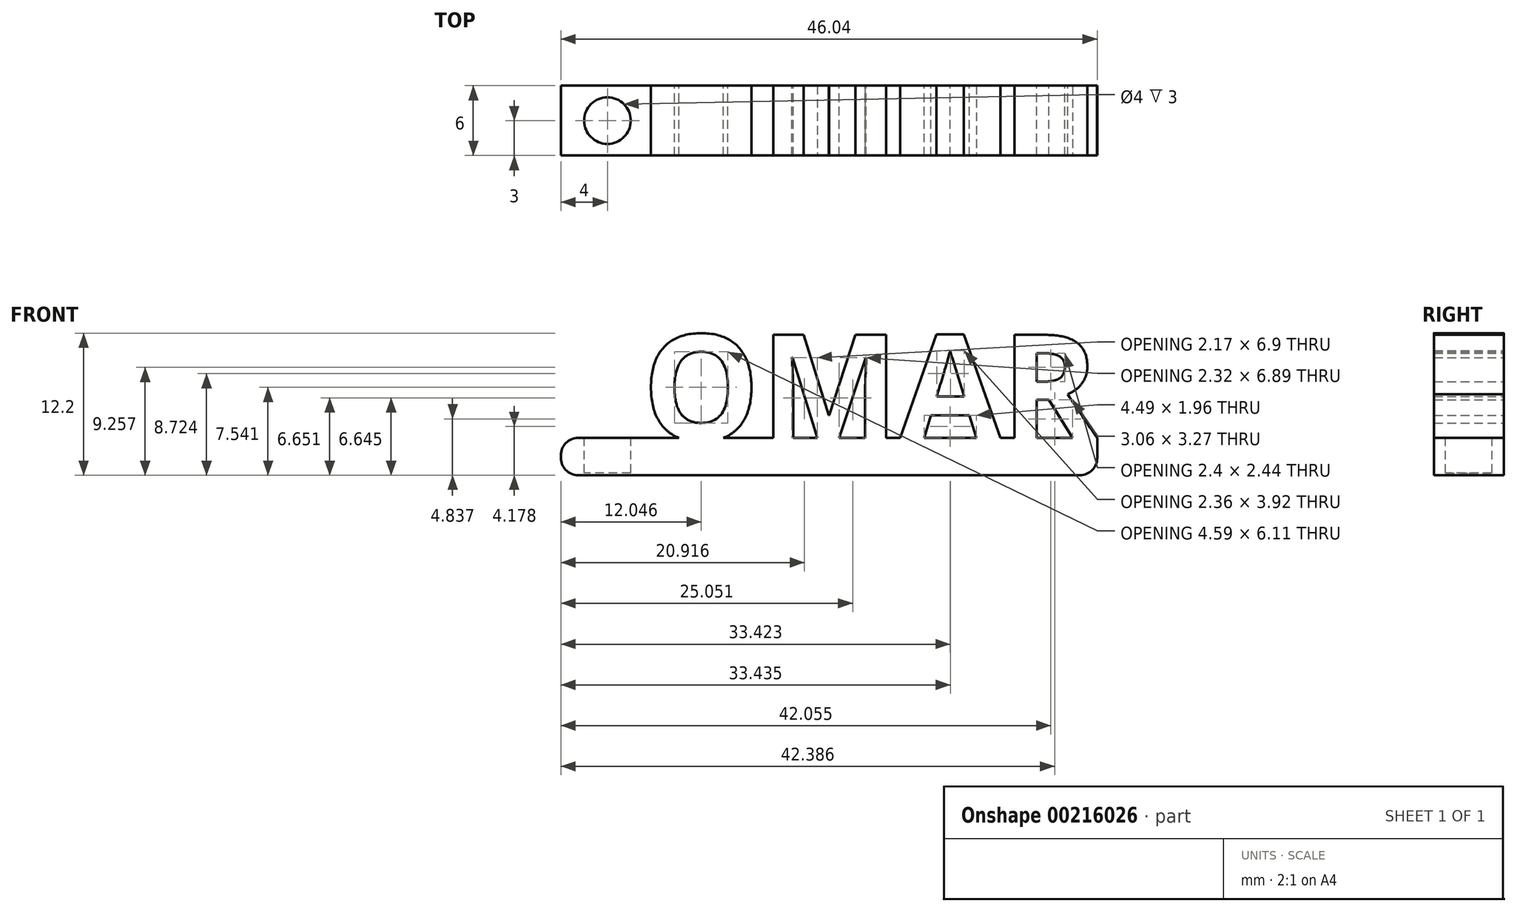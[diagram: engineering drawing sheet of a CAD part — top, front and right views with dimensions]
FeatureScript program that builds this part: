
annotation { "Feature Type Name" : "Feature", "Feature Type Description" : "" }
export const myFeature = defineFeature(function(context is Context, id is Id, definition is map)
    precondition{}
    {
        {
            var Q0;
            Q0=qCreatedBy(makeId("Front.planeOp"),FACE);
            var sketch = newSketch(context, id + "F0", { "sketchPlane" : qUnion([Q0])});
            skText(sketch, "E0", { "text": "OMAR", "fontName": "OpenSans-Bold.ttf"});
            const initialGuessF0  = {"E0": [-0.02, 0, 1, 0, 0.00913]};
            skSetInitialGuess(sketch, initialGuessF0);
            skSolve(sketch);
        }
        {
            var Q0;
            Q0=qCreatedBy(makeId("Top.planeOp"),FACE);
            var sketch = newSketch(context, id + "F1", { "sketchPlane" : qUnion([Q0])});
            skLineSegment(sketch, "E1.bottom", {"start": v(-20, 3) * mm, "end": v(19.04, 3) * mm});
            skLineSegment(sketch, "E1.top", {"start": v(-20, -3) * mm, "end": v(19.04, -3) * mm});
            skLineSegment(sketch, "E1.left", {"start": v(-20, 3) * mm, "end": v(-20, -3) * mm});
            skLineSegment(sketch, "E1.right", {"start": v(19.04, 3) * mm, "end": v(19.04, -3) * mm});
            skSolve(sketch);
        }
        {
            var Q0;
            Q0 = qSketchRegion(id + "F0", true);
            extrude(context, id + "F2", {"entities" : qUnion([Q0]), "endBound" : BoundingType.SYMMETRIC, "depth" : 6 * mm});
        }
        {
            var Q0;
            Q0=makeQuery(id+"F1.imprint","IMPRINT",FACE,{"disambiguationData":[TD([[makeQuery(id+"F1.imprint","IMPRINT",EDGE,{"derivedFrom":sQuery(id+"F1.wireOp",EDGE,"E1.bottom")}),-1.0]])]});
            extrude(context, id + "F3", {"entities" : qUnion([Q0]), "depth" : 0.2 * mm});
        }
        {
            var Q0;
            Q0=makeQuery(id+"F3.opExtrude","CAP_FACE",FACE,{"disambiguationData":[OSD([sQuery(id+"F1.wireOp",EDGE,"E1.bottom"),sQuery(id+"F1.wireOp",EDGE,"E1.top"),sQuery(id+"F1.wireOp",EDGE,"E1.left"),sQuery(id+"F1.wireOp",EDGE,"E1.right")])],"isStart":true});
            extrude(context, id + "F4", {"entities" : qUnion([Q0]), "depth" : 3 * mm});
        }
        {
            var Q0;
            Q0=makeQuery(id+"F3.opExtrude","SWEPT_BODY",BODY,{"disambiguationData":[OSD([sQuery(id+"F1.wireOp",EDGE,"E1.bottom"),sQuery(id+"F1.wireOp",EDGE,"E1.top"),sQuery(id+"F1.wireOp",EDGE,"E1.left"),sQuery(id+"F1.wireOp",EDGE,"E1.right")])]});
            var Q1;
            Q1=makeQuery(id+"F4.opExtrude","SWEPT_BODY",BODY,{"disambiguationData":[OSD([sQuery(id+"F1.wireOp",EDGE,"E1.bottom"),sQuery(id+"F1.wireOp",EDGE,"E1.top"),sQuery(id+"F1.wireOp",EDGE,"E1.left"),sQuery(id+"F1.wireOp",EDGE,"E1.right")])]});
            var Q2;
            Q2=makeQuery(id+"F2.opExtrude","SWEPT_BODY",BODY,{"disambiguationData":[OSD([sQuery(id+"F0.wireOp",EDGE,"E0.sketch_text.stroke-45"),sQuery(id+"F0.wireOp",EDGE,"E0.sketch_text.stroke-46"),sQuery(id+"F0.wireOp",EDGE,"E0.sketch_text.stroke-47"),sQuery(id+"F0.wireOp",EDGE,"E0.sketch_text.stroke-48"),sQuery(id+"F0.wireOp",EDGE,"E0.sketch_text.stroke-49"),sQuery(id+"F0.wireOp",EDGE,"E0.sketch_text.stroke-50"),sQuery(id+"F0.wireOp",EDGE,"E0.sketch_text.stroke-51"),sQuery(id+"F0.wireOp",EDGE,"E0.sketch_text.stroke-52"),sQuery(id+"F0.wireOp",EDGE,"E0.sketch_text.stroke-53"),sQuery(id+"F0.wireOp",EDGE,"E0.sketch_text.stroke-54"),sQuery(id+"F0.wireOp",EDGE,"E0.sketch_text.stroke-55"),sQuery(id+"F0.wireOp",EDGE,"E0.sketch_text.stroke-56"),sQuery(id+"F0.wireOp",EDGE,"E0.sketch_text.stroke-57"),sQuery(id+"F0.wireOp",EDGE,"E0.sketch_text.stroke-58"),sQuery(id+"F0.wireOp",EDGE,"E0.sketch_text.stroke-59"),sQuery(id+"F0.wireOp",EDGE,"E0.sketch_text.stroke-60"),sQuery(id+"F0.wireOp",EDGE,"E0.sketch_text.stroke-61"),sQuery(id+"F0.wireOp",EDGE,"E0.sketch_text.stroke-62"),sQuery(id+"F0.wireOp",EDGE,"E0.sketch_text.stroke-63")])]});
            var Q3;
            Q3=makeQuery(id+"F2.opExtrude","SWEPT_BODY",BODY,{"disambiguationData":[OSD([sQuery(id+"F0.wireOp",EDGE,"E0.sketch_text.stroke-14"),sQuery(id+"F0.wireOp",EDGE,"E0.sketch_text.stroke-15"),sQuery(id+"F0.wireOp",EDGE,"E0.sketch_text.stroke-16"),sQuery(id+"F0.wireOp",EDGE,"E0.sketch_text.stroke-17"),sQuery(id+"F0.wireOp",EDGE,"E0.sketch_text.stroke-18"),sQuery(id+"F0.wireOp",EDGE,"E0.sketch_text.stroke-19"),sQuery(id+"F0.wireOp",EDGE,"E0.sketch_text.stroke-20"),sQuery(id+"F0.wireOp",EDGE,"E0.sketch_text.stroke-21"),sQuery(id+"F0.wireOp",EDGE,"E0.sketch_text.stroke-22"),sQuery(id+"F0.wireOp",EDGE,"E0.sketch_text.stroke-23"),sQuery(id+"F0.wireOp",EDGE,"E0.sketch_text.stroke-24"),sQuery(id+"F0.wireOp",EDGE,"E0.sketch_text.stroke-25"),sQuery(id+"F0.wireOp",EDGE,"E0.sketch_text.stroke-26"),sQuery(id+"F0.wireOp",EDGE,"E0.sketch_text.stroke-27"),sQuery(id+"F0.wireOp",EDGE,"E0.sketch_text.stroke-28"),sQuery(id+"F0.wireOp",EDGE,"E0.sketch_text.stroke-29"),sQuery(id+"F0.wireOp",EDGE,"E0.sketch_text.stroke-30"),sQuery(id+"F0.wireOp",EDGE,"E0.sketch_text.stroke-31"),sQuery(id+"F0.wireOp",EDGE,"E0.sketch_text.stroke-32")])]});
            var Q4;
            Q4=makeQuery(id+"F2.opExtrude","SWEPT_BODY",BODY,{"disambiguationData":[OSD([sQuery(id+"F0.wireOp",EDGE,"E0.sketch_text.stroke-0"),sQuery(id+"F0.wireOp",EDGE,"E0.sketch_text.stroke-1"),sQuery(id+"F0.wireOp",EDGE,"E0.sketch_text.stroke-2"),sQuery(id+"F0.wireOp",EDGE,"E0.sketch_text.stroke-3"),sQuery(id+"F0.wireOp",EDGE,"E0.sketch_text.stroke-4"),sQuery(id+"F0.wireOp",EDGE,"E0.sketch_text.stroke-5"),sQuery(id+"F0.wireOp",EDGE,"E0.sketch_text.stroke-6"),sQuery(id+"F0.wireOp",EDGE,"E0.sketch_text.stroke-7"),sQuery(id+"F0.wireOp",EDGE,"E0.sketch_text.stroke-8"),sQuery(id+"F0.wireOp",EDGE,"E0.sketch_text.stroke-9"),sQuery(id+"F0.wireOp",EDGE,"E0.sketch_text.stroke-10"),sQuery(id+"F0.wireOp",EDGE,"E0.sketch_text.stroke-11"),sQuery(id+"F0.wireOp",EDGE,"E0.sketch_text.stroke-12"),sQuery(id+"F0.wireOp",EDGE,"E0.sketch_text.stroke-13")])]});
            var Q5;
            Q5=makeQuery(id+"F2.opExtrude","SWEPT_BODY",BODY,{"disambiguationData":[OSD([sQuery(id+"F0.wireOp",EDGE,"E0.sketch_text.stroke-33"),sQuery(id+"F0.wireOp",EDGE,"E0.sketch_text.stroke-34"),sQuery(id+"F0.wireOp",EDGE,"E0.sketch_text.stroke-35"),sQuery(id+"F0.wireOp",EDGE,"E0.sketch_text.stroke-36"),sQuery(id+"F0.wireOp",EDGE,"E0.sketch_text.stroke-37"),sQuery(id+"F0.wireOp",EDGE,"E0.sketch_text.stroke-38"),sQuery(id+"F0.wireOp",EDGE,"E0.sketch_text.stroke-39"),sQuery(id+"F0.wireOp",EDGE,"E0.sketch_text.stroke-40"),sQuery(id+"F0.wireOp",EDGE,"E0.sketch_text.stroke-41"),sQuery(id+"F0.wireOp",EDGE,"E0.sketch_text.stroke-42"),sQuery(id+"F0.wireOp",EDGE,"E0.sketch_text.stroke-43"),sQuery(id+"F0.wireOp",EDGE,"E0.sketch_text.stroke-44")])]});
            booleanBodies(context, id + "F5", {"operationType" : BooleanOperationType.UNION, "tools" : qUnion([Q0, Q1, Q2, Q3, Q4, Q5])});
        }
        {
            var Q0;
            {var subQ0=sQuery(id+"F1.wireOp",EDGE,"E1.left");Q0=makeQuery(id+"F5.opBoolean","MERGE",FACE,{"derivedFrom":[makeQuery(id+"F3.opExtrude","SWEPT_FACE",FACE,{"disambiguationData":[OSD([subQ0])]}),makeQuery(id+"F4.opExtrude","SWEPT_FACE",FACE,{"disambiguationData":[OSD([subQ0])]})]});}
            var sketch = newSketch(context, id + "F6", { "sketchPlane" : qUnion([Q0])});
            skLineSegment(sketch, "E2.bottom", {"start": v(-3, -3) * mm, "end": v(3, -3) * mm});
            skLineSegment(sketch, "E2.top", {"start": v(-3, 0.2) * mm, "end": v(3, 0.2) * mm});
            skLineSegment(sketch, "E2.left", {"start": v(-3, -3) * mm, "end": v(-3, 0.2) * mm});
            skLineSegment(sketch, "E2.right", {"start": v(3, -3) * mm, "end": v(3, 0.2) * mm});
            skSolve(sketch);
        }
        {
            var Q0;
            Q0 = qSketchRegion(id + "F6", true);
            extrude(context, id + "F7", {"entities" : qUnion([Q0]), "operationType" : NewBodyOperationType.ADD, "depth" : 7 * mm});
        }
        {
            var Q0;
            Q0=makeQuery(id+"F7.opExtrude","CAP_EDGE",EDGE,{"disambiguationData":[OSD([sQuery(id+"F6.wireOp",EDGE,"E2.bottom")])],"isStart":false});
            var Q1;
            Q1=makeQuery(id+"F7.opExtrude","CAP_EDGE",EDGE,{"disambiguationData":[OSD([sQuery(id+"F6.wireOp",EDGE,"E2.top")])],"isStart":false});
            var Q2;
            Q2=makeQuery(id+"F4.opExtrude","CAP_EDGE",EDGE,{"disambiguationData":[OSD([sQuery(id+"F1.wireOp",EDGE,"E1.right")])],"isStart":false});
            fillet(context, id + "F8", {"entities" : qUnion([Q0, Q1, Q2]), "radius" : 1.5 * mm, "tangentPropagation" : true, "allowEdgeOverflow" : false});
        }
        {
            var Q0;
            {var subQ19=sQuery(id+"F1.wireOp",EDGE,"E1.top");var subQ20=sQuery(id+"F1.wireOp",EDGE,"E1.bottom");var subQ63=sQuery(id+"F0.wireOp",EDGE,"E0.sketch_text.stroke-2");var subQ66=sQuery(id+"F1.wireOp",EDGE,"E1.left");Q0=makeQuery(id+"F7.boolean.opBoolean","MERGE",FACE,{"derivedFrom":[makeQuery(id+"F5.opBoolean","SPLIT",FACE,{"disambiguationData":[TD([makeQuery(id+"F2.opExtrude","SWEPT_FACE",FACE,{"disambiguationData":[OSD([subQ63])]})])],"derivedFrom":makeQuery(id+"F3.opExtrude","CAP_FACE",FACE,{"disambiguationData":[OSD([subQ20,subQ19,subQ66,sQuery(id+"F1.wireOp",EDGE,"E1.right")])],"isStart":false})}),makeQuery(id+"F7.opExtrude","SWEPT_FACE",FACE,{"disambiguationData":[OSD([sQuery(id+"F6.wireOp",EDGE,"E2.top")])]})]});}
            var sketch = newSketch(context, id + "F9", { "sketchPlane" : qUnion([Q0])});
            skCircle(sketch, "E3", {"center": v(-23, 0) * mm, "radius": 2 * mm});
            skSolve(sketch);
        }
        {
            var Q0;
            Q0=makeQuery(id+"F9.imprint","IMPRINT",FACE,{"disambiguationData":[TD([[makeQuery(id+"F9.imprint","IMPRINT",EDGE,{"derivedFrom":sQuery(id+"F9.wireOp",EDGE,"E3")}),1.0]])]});
            extrude(context, id + "F10", {"entities" : qUnion([Q0]), "operationType" : NewBodyOperationType.REMOVE, "oppositeDirection" : true, "depth" : 3 * mm});
        }
        {
            var Q0;
            {var subQ0=sQuery(id+"F1.wireOp",EDGE,"E1.top");Q0=makeQuery(id+"F7.boolean.opBoolean","MERGE",FACE,{"derivedFrom":[makeQuery(id+"F5.opBoolean","MERGE",FACE,{"derivedFrom":[makeQuery(id+"F2.opExtrude","CAP_FACE",FACE,{"disambiguationData":[OSD([sQuery(id+"F0.wireOp",EDGE,"E0.sketch_text.stroke-0"),sQuery(id+"F0.wireOp",EDGE,"E0.sketch_text.stroke-1"),sQuery(id+"F0.wireOp",EDGE,"E0.sketch_text.stroke-2"),sQuery(id+"F0.wireOp",EDGE,"E0.sketch_text.stroke-3"),sQuery(id+"F0.wireOp",EDGE,"E0.sketch_text.stroke-4"),sQuery(id+"F0.wireOp",EDGE,"E0.sketch_text.stroke-5"),sQuery(id+"F0.wireOp",EDGE,"E0.sketch_text.stroke-6"),sQuery(id+"F0.wireOp",EDGE,"E0.sketch_text.stroke-7"),sQuery(id+"F0.wireOp",EDGE,"E0.sketch_text.stroke-8"),sQuery(id+"F0.wireOp",EDGE,"E0.sketch_text.stroke-9"),sQuery(id+"F0.wireOp",EDGE,"E0.sketch_text.stroke-10"),sQuery(id+"F0.wireOp",EDGE,"E0.sketch_text.stroke-11"),sQuery(id+"F0.wireOp",EDGE,"E0.sketch_text.stroke-12"),sQuery(id+"F0.wireOp",EDGE,"E0.sketch_text.stroke-13")])],"isStart":false}),makeQuery(id+"F2.opExtrude","CAP_FACE",FACE,{"disambiguationData":[OSD([sQuery(id+"F0.wireOp",EDGE,"E0.sketch_text.stroke-14"),sQuery(id+"F0.wireOp",EDGE,"E0.sketch_text.stroke-15"),sQuery(id+"F0.wireOp",EDGE,"E0.sketch_text.stroke-16"),sQuery(id+"F0.wireOp",EDGE,"E0.sketch_text.stroke-17"),sQuery(id+"F0.wireOp",EDGE,"E0.sketch_text.stroke-18"),sQuery(id+"F0.wireOp",EDGE,"E0.sketch_text.stroke-19"),sQuery(id+"F0.wireOp",EDGE,"E0.sketch_text.stroke-20"),sQuery(id+"F0.wireOp",EDGE,"E0.sketch_text.stroke-21"),sQuery(id+"F0.wireOp",EDGE,"E0.sketch_text.stroke-22"),sQuery(id+"F0.wireOp",EDGE,"E0.sketch_text.stroke-23"),sQuery(id+"F0.wireOp",EDGE,"E0.sketch_text.stroke-24"),sQuery(id+"F0.wireOp",EDGE,"E0.sketch_text.stroke-25"),sQuery(id+"F0.wireOp",EDGE,"E0.sketch_text.stroke-26"),sQuery(id+"F0.wireOp",EDGE,"E0.sketch_text.stroke-27"),sQuery(id+"F0.wireOp",EDGE,"E0.sketch_text.stroke-28"),sQuery(id+"F0.wireOp",EDGE,"E0.sketch_text.stroke-29"),sQuery(id+"F0.wireOp",EDGE,"E0.sketch_text.stroke-30"),sQuery(id+"F0.wireOp",EDGE,"E0.sketch_text.stroke-31"),sQuery(id+"F0.wireOp",EDGE,"E0.sketch_text.stroke-32")])],"isStart":false}),makeQuery(id+"F2.opExtrude","CAP_FACE",FACE,{"disambiguationData":[OSD([sQuery(id+"F0.wireOp",EDGE,"E0.sketch_text.stroke-33"),sQuery(id+"F0.wireOp",EDGE,"E0.sketch_text.stroke-34"),sQuery(id+"F0.wireOp",EDGE,"E0.sketch_text.stroke-35"),sQuery(id+"F0.wireOp",EDGE,"E0.sketch_text.stroke-36"),sQuery(id+"F0.wireOp",EDGE,"E0.sketch_text.stroke-37"),sQuery(id+"F0.wireOp",EDGE,"E0.sketch_text.stroke-38"),sQuery(id+"F0.wireOp",EDGE,"E0.sketch_text.stroke-39"),sQuery(id+"F0.wireOp",EDGE,"E0.sketch_text.stroke-40"),sQuery(id+"F0.wireOp",EDGE,"E0.sketch_text.stroke-41"),sQuery(id+"F0.wireOp",EDGE,"E0.sketch_text.stroke-42"),sQuery(id+"F0.wireOp",EDGE,"E0.sketch_text.stroke-43"),sQuery(id+"F0.wireOp",EDGE,"E0.sketch_text.stroke-44")])],"isStart":false}),makeQuery(id+"F2.opExtrude","CAP_FACE",FACE,{"disambiguationData":[OSD([sQuery(id+"F0.wireOp",EDGE,"E0.sketch_text.stroke-45"),sQuery(id+"F0.wireOp",EDGE,"E0.sketch_text.stroke-46"),sQuery(id+"F0.wireOp",EDGE,"E0.sketch_text.stroke-47"),sQuery(id+"F0.wireOp",EDGE,"E0.sketch_text.stroke-48"),sQuery(id+"F0.wireOp",EDGE,"E0.sketch_text.stroke-49"),sQuery(id+"F0.wireOp",EDGE,"E0.sketch_text.stroke-50"),sQuery(id+"F0.wireOp",EDGE,"E0.sketch_text.stroke-51"),sQuery(id+"F0.wireOp",EDGE,"E0.sketch_text.stroke-52"),sQuery(id+"F0.wireOp",EDGE,"E0.sketch_text.stroke-53"),sQuery(id+"F0.wireOp",EDGE,"E0.sketch_text.stroke-54"),sQuery(id+"F0.wireOp",EDGE,"E0.sketch_text.stroke-55"),sQuery(id+"F0.wireOp",EDGE,"E0.sketch_text.stroke-56"),sQuery(id+"F0.wireOp",EDGE,"E0.sketch_text.stroke-57"),sQuery(id+"F0.wireOp",EDGE,"E0.sketch_text.stroke-58"),sQuery(id+"F0.wireOp",EDGE,"E0.sketch_text.stroke-59"),sQuery(id+"F0.wireOp",EDGE,"E0.sketch_text.stroke-60"),sQuery(id+"F0.wireOp",EDGE,"E0.sketch_text.stroke-61"),sQuery(id+"F0.wireOp",EDGE,"E0.sketch_text.stroke-62"),sQuery(id+"F0.wireOp",EDGE,"E0.sketch_text.stroke-63")])],"isStart":false}),makeQuery(id+"F3.opExtrude","SWEPT_FACE",FACE,{"disambiguationData":[OSD([subQ0])]}),makeQuery(id+"F4.opExtrude","SWEPT_FACE",FACE,{"disambiguationData":[OSD([subQ0])]})]}),makeQuery(id+"F7.opExtrude","SWEPT_FACE",FACE,{"disambiguationData":[OSD([sQuery(id+"F6.wireOp",EDGE,"E2.right")])]})]});}
            var sketch = newSketch(context, id + "F11", { "sketchPlane" : qUnion([Q0])});
            skLineSegment(sketch, "E4", {"start": v(19.04, 0) * mm, "end": v(19.18, 0) * mm});
            skLineSegment(sketch, "E5", {"start": v(19.18, 0) * mm, "end": v(19.04, 0.2) * mm});
            skLineSegment(sketch, "E6", {"start": v(19.04, 0.2) * mm, "end": v(19.04, 0) * mm});
            skSolve(sketch);
        }
        {
            var Q0;
            {var subQ0=sQuery(id+"F11.wireOp",EDGE,"E4");Q0=makeQuery(id+"F11.imprint","IMPRINT",FACE,{"disambiguationData":[TD([[makeQuery(id+"F11.imprint","IMPRINT",EDGE,{"derivedFrom":subQ0}),-1.0]])]});}
            extrude(context, id + "F12", {"entities" : qUnion([Q0]), "operationType" : NewBodyOperationType.REMOVE, "oppositeDirection" : true, "depth" : 6 * mm});
        }
    });
